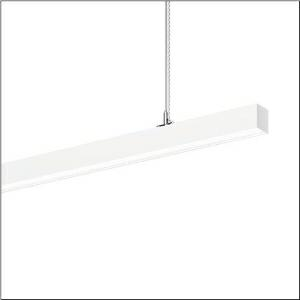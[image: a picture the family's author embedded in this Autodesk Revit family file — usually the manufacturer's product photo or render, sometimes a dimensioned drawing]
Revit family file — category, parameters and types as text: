
# Revit family: silica_r__21_51mx33tctdw_01d4
name_source: partatom
category: Lighting Fixtures
units: mm (PartAtom-declared; Revit-internal decimal feet)

## family parameters
Cut with Voids When Loaded = No
Host = Face
Light Source = No
Part Type = Normal
Room Calculation Point = No
Round Connector Dimension = Use Diameter
Shared = No

## types (1)
- --- (1 x LED, 14340 lm, 134.7 W, 6500K)
    Apparent Load = 135 VA
    CIE Flux Codes = 78 96 99 56 100
    Color Rendering = 80
    Color Temperature = 6500K
    Default Elevation = 1800 mm
    Description = Silica® 21, office luminaire, primary optical cover: prismatic diffuser, of PMMA, CAT 2 (L<= 3000cd/m²), light emission: direct/indirect distribution, primary light characteristic: symmetric, installation type: suspended mounting, LED, rated luminous flux: 14.340lm, luminous efficacy: 101lm/W, light colour: 8tw, colour temperature: 2700..6500K, control gear: ECG DALI, with terminal, 3+2-pole, max. 2.5mm², mains connection: 220..240V, AC, 50/60Hz, rated input power: 141.4W, luminaire housing, of aluminium, traffic white (RAL 9016), length: 3.004mm, width: 53mm, height: 53mm, protection rating (complete): IP20, insulation class (complete): insulation class I (protective earthing), certification: CE, permissible operating ambient temperature: 0..+35°C, standard: EN 50419, packaging unit: 1 piece
    Height = 53 mm
    Lamp = 1 x LED
    Lamp Light Flux = 14340 lm
    Lamp Power = 134.7 W
    Lamp count = 1
    Length = 3004 mm
    Luminous efficacy = 106 lm/W
    Manufacturer = Siteco
    ModVariant = No
    Model = 51MX33TCTDW
    Mounting Place = Ceiling
    Mounting Type = Pendant
    Number of Poles = 1
    OnlyDefault = Yes
    Power Factor = 1
    Product Name = Silica® 21
    Product group = office luminaire | ceiling pendant
    ProductGroupID = 905
    Protection Class = Protection class I
    Protection Degree = IP 20
    RLX_Detail_Level = 1
    RlxData = <blob elided: 18101 chars, md5=56b5d86a>
    Socket = socket
    Standby Power = 0 W
    System Light Flux = 14340 lm
    System Power = 135 W
    Type Comments = individual setting
    Type Image = l_1251642.jpg
    URL = http://relux.com
    VarID = @adj_045861
    Voltage = 0 V
    Weight = 0.00 kg
    Width = 53 mm

## geometry (parser evidence)
native form markers: Blend x4, Sweep x11
no freeform markers — native parametric forms only
